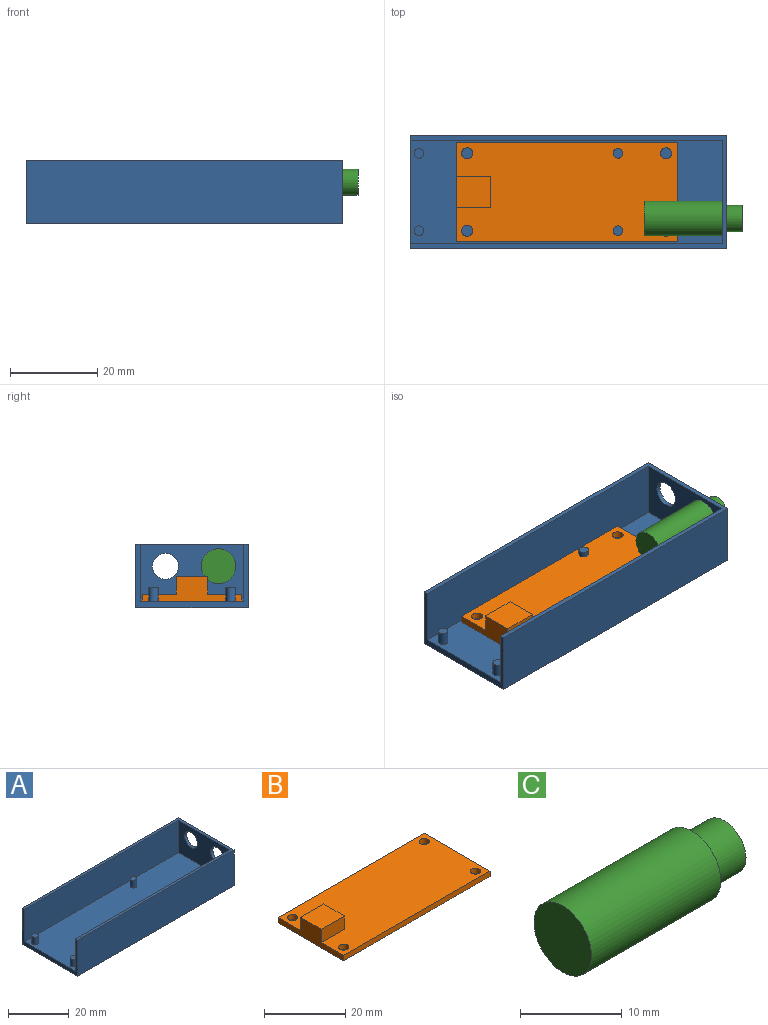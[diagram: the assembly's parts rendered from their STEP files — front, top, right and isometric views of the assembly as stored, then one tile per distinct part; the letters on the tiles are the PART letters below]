
ASSEMBLY  parts=3 mates=2
PART A: 20 faces, bbox 72.8x25.9x14.5 mm
  f0: plane 25.86x14.5mm, normal (1,0,0), area 318.4mm2, adj f3,f4,f6,f9,f18,f19
  f1: plane 23.86x13mm, normal (-1,0,0), area 253.6mm2, adj f2,f7,f8,f9,f18,f19
  f2: plane 71.8x23.86mm, normal (0,0,1), area 1697.9mm2, adj f1,f5,f7,f8,f10,f12,f14,f16
  f3: plane 72.8x14.5mm, normal (0,-1,0), area 1055.6mm2, adj f0,f5,f6,f9
  f4: plane 72.8x14.5mm, normal (0,1,0), area 1055.6mm2, adj f0,f5,f6,f9
  f5: plane 25.86x14.5mm, normal (-1,0,0), area 64.8mm2, adj f2,f3,f4,f6,f7,f8,f9
  f6: plane 72.8x25.86mm, normal (0,0,-1), area 1882.6mm2, adj f0,f3,f4,f5
  f7: plane 71.8x13mm, normal (0,-1,0), area 933.4mm2, adj f1,f2,f5,f9
  f8: plane 71.8x13mm, normal (0,1,0), area 933.4mm2, adj f1,f2,f5,f9
  f9: plane 72.8x25.86mm, normal (0,0,1), area 169.5mm2, adj f0,f1,f3,f4,f5,f7,f8
  f10: cylinder r=1.1mm len=3mm, axis (0,0,-1), area 20.7mm2, adj f2,f11
  f11: plane 2.2x2.2mm, normal (0,0,1), area 3.8mm2, adj f10
  f12: cylinder r=1.1mm len=3mm, axis (0,0,-1), area 20.7mm2, adj f2,f13
  f13: plane 2.2x2.2mm, normal (0,0,1), area 3.8mm2, adj f12
  f14: cylinder r=1.1mm len=3mm, axis (0,0,-1), area 20.7mm2, adj f2,f15
  f15: plane 2.2x2.2mm, normal (0,0,1), area 3.8mm2, adj f14
  f16: cylinder r=1.1mm len=3mm, axis (0,0,-1), area 20.7mm2, adj f2,f17
  f17: plane 2.2x2.2mm, normal (0,0,1), area 3.8mm2, adj f16
  f18: cylinder r=3mm len=6mm, axis (1,0,0), area 18.8mm2, adj f0,f1
  f19: cylinder r=3mm len=6mm, axis (1,0,0), area 18.8mm2, adj f0,f1
PART B: 14 faces, bbox 50.8x22.9x5.6 mm
  f0: plane 50.8x22.86mm, normal (0,0,1), area 1083.3mm2, adj f1,f2,f3,f4,f6,f7,f8,f9
  f1: plane 50.8x1.6mm, normal (0,-1,0), area 81.3mm2, adj f0,f2,f4,f5
  f2: plane 22.86x1.6mm, normal (1,0,0), area 36.6mm2, adj f0,f1,f3,f5
  f3: plane 50.8x1.6mm, normal (0,1,0), area 81.3mm2, adj f0,f2,f4,f5
  f4: plane 22.86x5.6mm, normal (-1,0,0), area 65.5mm2, adj f0,f1,f3,f5,f10,f12,f13
  f5: plane 50.8x22.86mm, normal (0,0,-1), area 1141mm2, adj f1,f2,f3,f4,f6,f7,f8,f9
  f6: cylinder r=1.27mm len=2.54mm, axis (0,0,1), area 12.8mm2, adj f0,f5
  f7: cylinder r=1.27mm len=2.54mm, axis (0,0,1), area 12.8mm2, adj f0,f5
  f8: cylinder r=1.27mm len=2.54mm, axis (0,0,1), area 12.8mm2, adj f0,f5
  f9: cylinder r=1.27mm len=2.54mm, axis (0,0,1), area 12.8mm2, adj f0,f5
  f10: plane 8x4mm, normal (0,-1,0), area 32mm2, adj f0,f4,f11,f13
  f11: plane 7.22x4mm, normal (1,0,0), area 28.9mm2, adj f0,f10,f12,f13
  f12: plane 8x4mm, normal (0,1,0), area 32mm2, adj f0,f4,f11,f13
  f13: plane 8x7.22mm, normal (0,0,1), area 57.8mm2, adj f4,f10,f11,f12
PART C: 5 faces, bbox 22.5x8x8 mm
  f0: cylinder r=4mm len=18mm, axis (-1,0,0), area 452.4mm2, adj f1,f2
  f1: plane 8x8mm, normal (1,0,0), area 22mm2, adj f0,f3
  f2: plane 8x8mm, normal (-1,0,0), area 50.3mm2, adj f0
  f3: cylinder r=3mm len=6mm, axis (-1,0,0), area 84.8mm2, adj f1,f4
  f4: plane 6x6mm, normal (1,0,0), area 28.3mm2, adj f3
PLACE A t=(-1.81,2.75,-0.05)mm fixed
PLACE B t=(-2.22,2.75,1.45)mm
PLACE C t=(15.59,-3.34,9.45)mm
MATE fastened C.f0 <-> A.f19  axis (-1,0,0) through (33.59,-3.34,9.45)mm
MATE fastened B.f5 <-> A.f2  axis (0,0,-1) through (-2.22,2.75,1.45)mm
